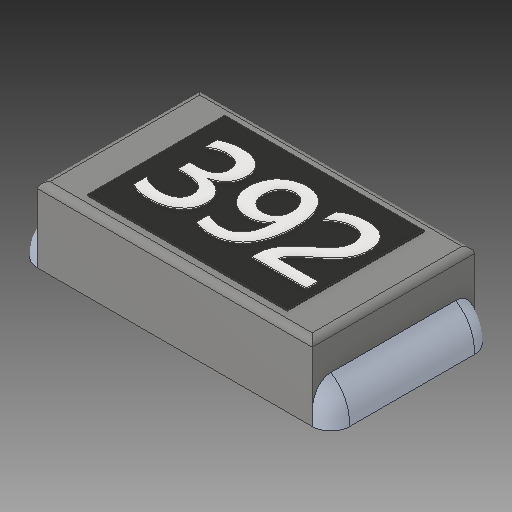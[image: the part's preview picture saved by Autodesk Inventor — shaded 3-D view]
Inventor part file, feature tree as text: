
AUTODESK INVENTOR PART (.ipt)
format: ipt  version: 2018.3 (Build 223284000, 284)  size: 307,200 bytes
history: native  units: mm
features: other x4, fillet x1, mirror x1
ambient origin geometry x8: Origin, YZ Plane, XZ Plane, XY Plane, X Axis, Y Axis, Z Axis, Center Point
bodies: Body1 (feature_tree), Body2 (feature_tree), Body3 (feature_tree)
feature tree (6):
  other  "Sólido1"
  other  "Sólido2"
  other  "Sólido3"
  fillet  "Fillet2"  [1 undecoded]
  mirror  "Mirror1"
  other  "Boss-Extrude4"
note: 1 required parameter value undecoded (feature->parameter linkage not recoverable at this tier; creation-order binding heuristic only, values carry confidence <= 0.55)
